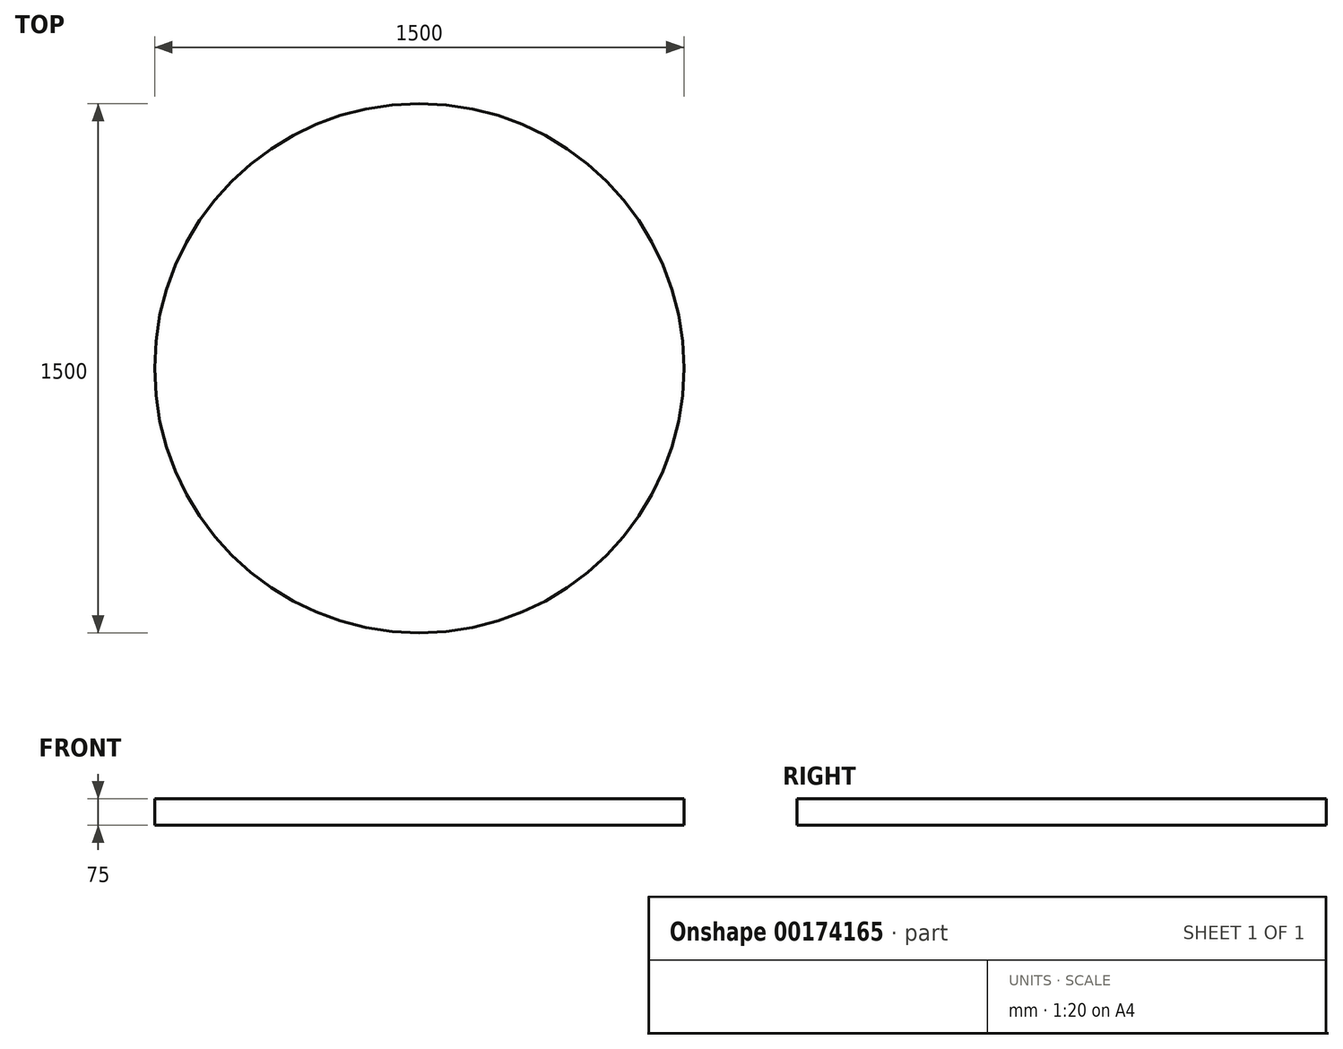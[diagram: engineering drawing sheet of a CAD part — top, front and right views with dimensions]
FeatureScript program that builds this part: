
annotation { "Feature Type Name" : "Feature", "Feature Type Description" : "" }
export const myFeature = defineFeature(function(context is Context, id is Id, definition is map)
    precondition{}
    {
        {
            var Q0;
            Q0=qCreatedBy(makeId("Top.planeOp"),FACE);
            var sketch = newSketch(context, id + "F0", { "sketchPlane" : qUnion([Q0])});
            skCircle(sketch, "E0", {"center": v(0, 0) * mm, "radius": 750 * mm});
            skSolve(sketch);
        }
        {
            var Q0;
            Q0=makeQuery(id+"F0.imprint","IMPRINT",FACE,{"disambiguationData":[TD([[makeQuery(id+"F0.imprint","IMPRINT",EDGE,{"derivedFrom":sQuery(id+"F0.wireOp",EDGE,"E0")}),1.0]])]});
            extrude(context, id + "F1", {"entities" : qUnion([Q0]), "oppositeDirection" : true, "depth" : 75 * mm});
        }
    });
